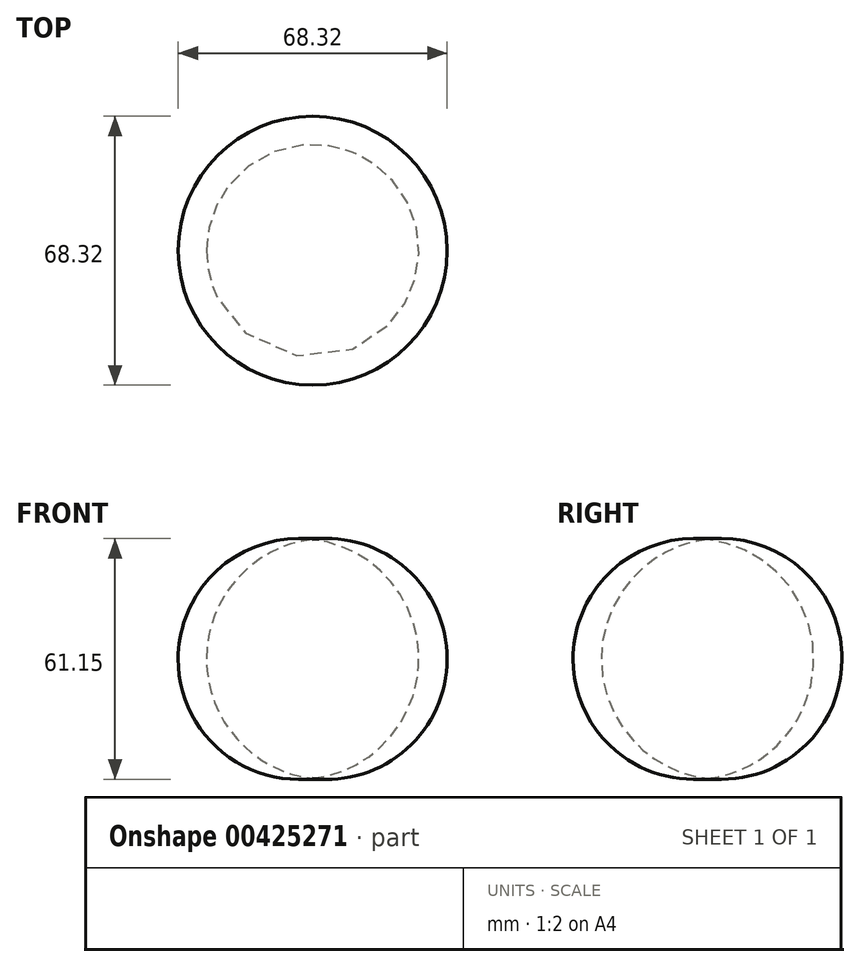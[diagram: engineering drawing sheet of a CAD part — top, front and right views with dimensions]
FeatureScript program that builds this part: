
annotation { "Feature Type Name" : "Feature", "Feature Type Description" : "" }
export const myFeature = defineFeature(function(context is Context, id is Id, definition is map)
    precondition{}
    {
        {
            var Q0;
            Q0=qCreatedBy(makeId("Front.planeOp"),FACE);
            var sketch = newSketch(context, id + "F0", { "sketchPlane" : qUnion([Q0])});
            skArc(sketch, "E0", {"start": v(0, -25.78) * mm, "mid": v(26.98, 4.58) * mm, "end": v(0, 34.94) * mm});
            skLineSegment(sketch, "E1", {"start": v(0, 34.94) * mm, "end": v(0, -25.78) * mm});
            skSolve(sketch);
        }
        {
            var Q0;
            Q0=makeQuery(id+"F0.imprint","IMPRINT",FACE,{"disambiguationData":[TD([[makeQuery(id+"F0.imprint","IMPRINT",EDGE,{"derivedFrom":sQuery(id+"F0.wireOp",EDGE,"E0")}),1.0]])]});
            var Q1;
            Q1=sQuery(id+"F0.wireOp",EDGE,"E1");
            revolve(context, id + "F1", {"entities" : qUnion([Q0]), "axis" : qUnion([Q1]), "revolveType" : RevolveType.FULL});
        }
    });
